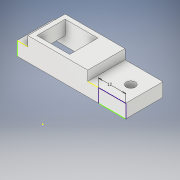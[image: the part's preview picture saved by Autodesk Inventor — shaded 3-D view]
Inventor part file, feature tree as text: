
AUTODESK INVENTOR PART (.ipt)
format: ipt  version: 2019 (Build 230136000, 136)  size: 192,512 bytes
history: native  units: in
note: dims shown in document units (in); Inventor stores cm internally (conversion verified against a paired STEP export)
features: extrude x4, sketch x4, plane x1, shell x1
ambient origin geometry x8: Origin, YZ Plane, XZ Plane, XY Plane, X Axis, Y Axis, Z Axis, Center Point
bodies: Solid3 (feature_tree)
feature tree (10):
  plane  "Work Plane1"
  extrude  "Extrusion1"  Depth=0.1575in
  shell  "Shell1"  Thickness=0.189in
  extrude  "Extrusion2"  Depth=0.0787in
  extrude  "Extrusion3"  Depth=0.3937in TaperAngle=0.0deg
  extrude  "Extrusion4"  Depth=0.1575in
  sketch  "Sketch1"  dims[d1=0.1575in d2=0.1575in d3=0.189in]
  sketch  "Sketch2"  dims[d4=0.4921in d5=0.0in d6=0.0787in]
  sketch  "Sketch3"  dims[d7=0.4921in d8=0.0in d10=0.3937in d11=0.0in]
  sketch  "Sketch5"  dims[d21=0.4724in d22=0.1575in d23=0.2362in d25=0.3248in d26=0.3937in d27=0.0in]
